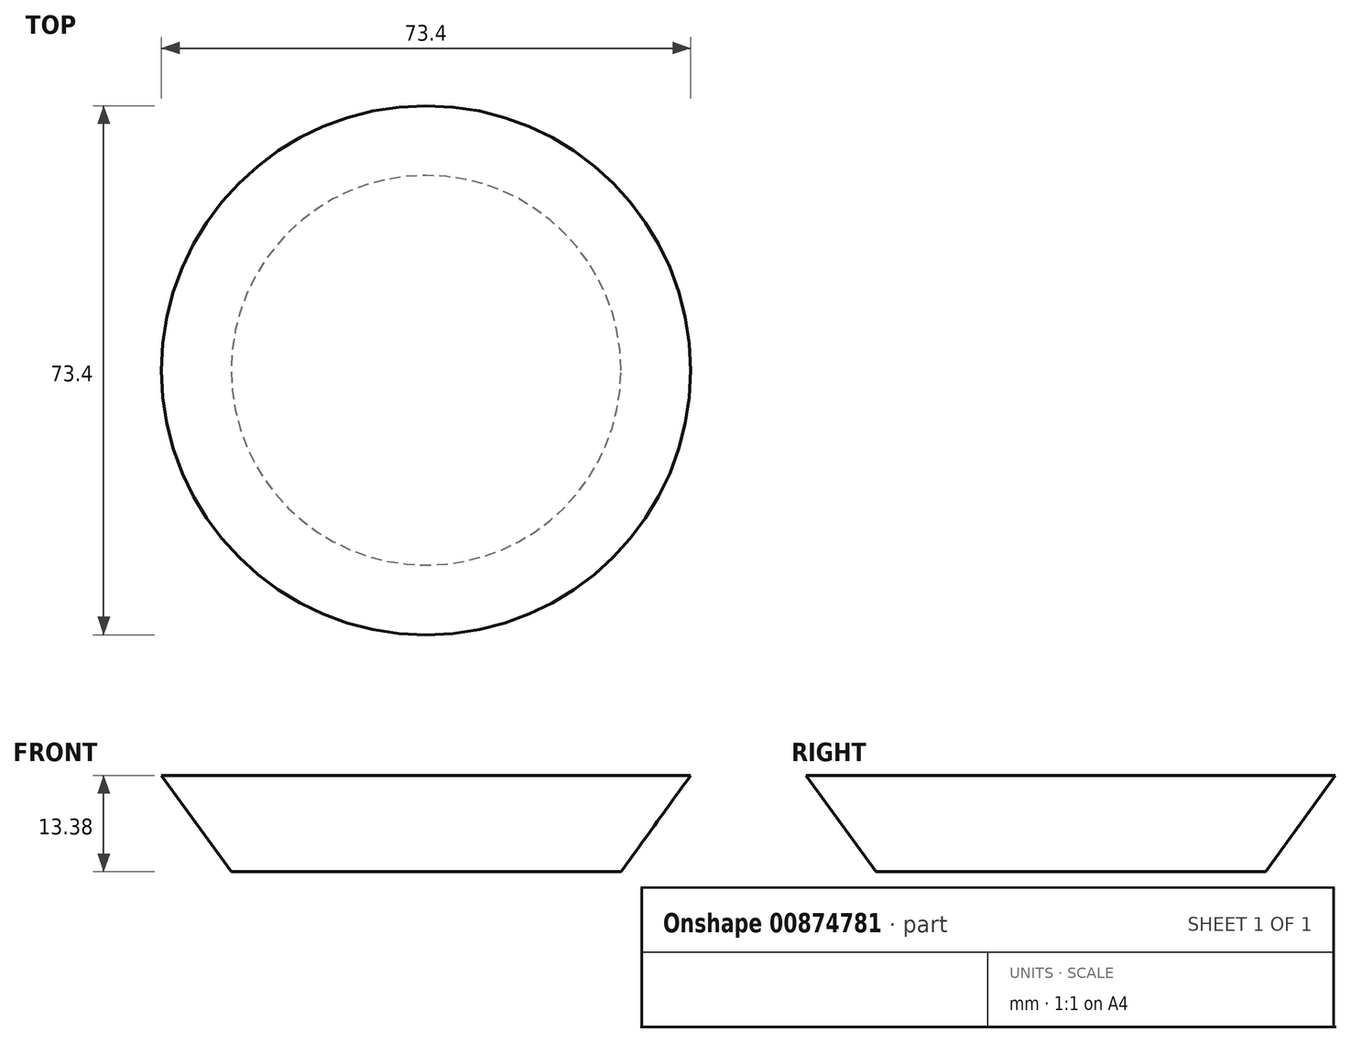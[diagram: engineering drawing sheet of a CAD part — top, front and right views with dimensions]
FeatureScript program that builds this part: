
annotation { "Feature Type Name" : "Feature", "Feature Type Description" : "" }
export const myFeature = defineFeature(function(context is Context, id is Id, definition is map)
    precondition{}
    {
        {
            var Q0;
            Q0=qCreatedBy(makeId("Front.planeOp"),FACE);
            var sketch = newSketch(context, id + "F0", { "sketchPlane" : qUnion([Q0])});
            skLineSegment(sketch, "E0", {"start": v(0, 0) * mm, "end": v(-27.03, 0) * mm});
            skLineSegment(sketch, "E1", {"start": v(-27.03, 0) * mm, "end": v(-36.7, 13.38) * mm});
            skLineSegment(sketch, "E2", {"start": v(-36.7, 13.38) * mm, "end": v(0, 13.38) * mm});
            skLineSegment(sketch, "E3", {"start": v(0, 13.38) * mm, "end": v(0, 0) * mm});
            skSolve(sketch);
        }
        {
            var Q0;
            Q0=makeQuery(id+"F0.imprint","IMPRINT",FACE,{"disambiguationData":[TD([[makeQuery(id+"F0.imprint","IMPRINT",EDGE,{"derivedFrom":sQuery(id+"F0.wireOp",EDGE,"E0")}),-1.0]])]});
            var Q1;
            Q1=sQuery(id+"F0.wireOp",EDGE,"E3");
            revolve(context, id + "F1", {"surfaceOperationType" : NewSurfaceOperationType.NEW, "entities" : qUnion([Q0]), "axis" : qUnion([Q1]), "revolveType" : RevolveType.FULL});
        }
    });
